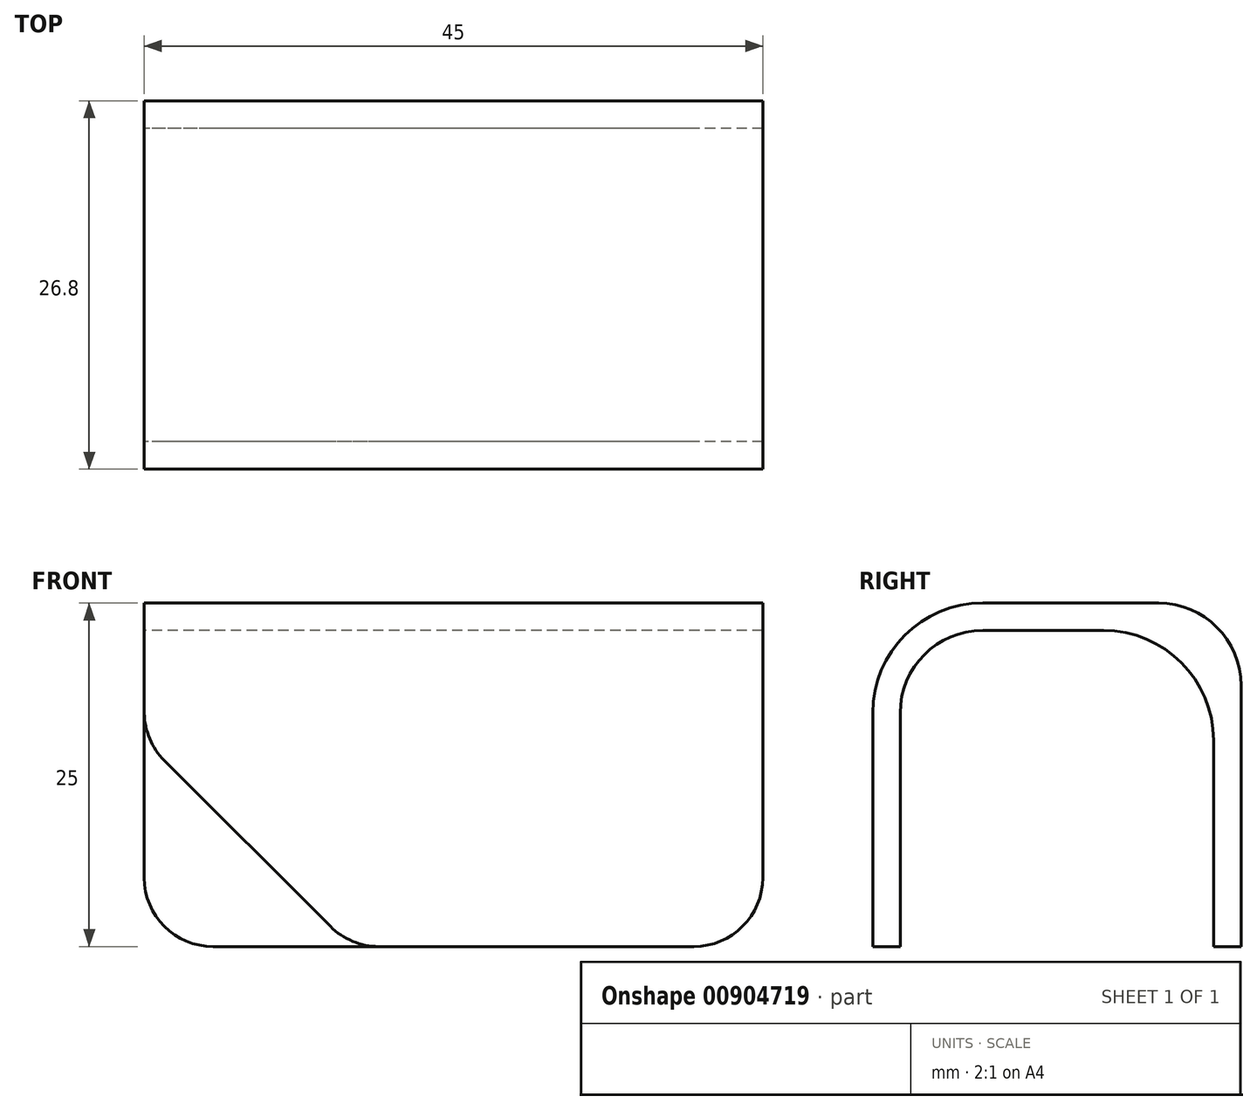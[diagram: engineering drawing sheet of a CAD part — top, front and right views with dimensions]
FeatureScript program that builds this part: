
annotation { "Feature Type Name" : "Feature", "Feature Type Description" : "" }
export const myFeature = defineFeature(function(context is Context, id is Id, definition is map)
    precondition{}
    {
        {
            var Q0;
            Q0=qCreatedBy(makeId("Right.planeOp"),FACE);
            var sketch = newSketch(context, id + "F0", { "sketchPlane" : qUnion([Q0])});
            skLineSegment(sketch, "E0.bottom", {"start": v(-13.4, 12.5) * mm, "end": v(13.4, 12.5) * mm});
            skLineSegment(sketch, "E0.top", {"start": v(-13.4, -12.5) * mm, "end": v(13.4, -12.5) * mm, "construction": true});
            skLineSegment(sketch, "E0.left", {"start": v(-13.4, 12.5) * mm, "end": v(-13.4, -12.5) * mm});
            skLineSegment(sketch, "E0.right", {"start": v(13.4, 12.5) * mm, "end": v(13.4, -12.5) * mm});
            skPoint(sketch, "E0.middle", {"position": v(0, 0) * mm});
            skLineSegment(sketch, "E1.0", {"start": v(11.4, 10.5) * mm, "end": v(11.4, -12.5) * mm});
            skLineSegment(sketch, "E1.1", {"start": v(-11.4, 10.5) * mm, "end": v(11.4, 10.5) * mm});
            skLineSegment(sketch, "E1.2", {"start": v(-11.4, 10.5) * mm, "end": v(-11.4, -12.5) * mm});
            skLineSegment(sketch, "E2", {"start": v(-11.4, -12.5) * mm, "end": v(-13.4, -12.5) * mm});
            skLineSegment(sketch, "E3", {"start": v(13.4, -12.5) * mm, "end": v(11.4, -12.5) * mm});
            skSolve(sketch);
        }
        {
            var Q0;
            Q0 = qSketchRegion(id + "F0", true);
            extrude(context, id + "F1", {"entities" : qUnion([Q0]), "depth" : 45 * mm, "offsetDistance" : 25 * mm});
        }
        {
            var Q0;
            Q0=makeQuery(id+"F1.opExtrude","SWEPT_EDGE",EDGE,{"disambiguationData":[OSD([sQuery(id+"F0.wireOp",EDGE,"E1.1"),sQuery(id+"F0.wireOp",EDGE,"E1.2")])]});
            fillet(context, id + "F2", {"entities" : qUnion([Q0]), "radius" : 6 * mm, "tangentPropagation" : true, "allowEdgeOverflow" : false});
        }
        {
            var Q0;
            Q0=makeQuery(id+"F1.opExtrude","SWEPT_EDGE",EDGE,{"disambiguationData":[OSD([sQuery(id+"F0.wireOp",EDGE,"E0.bottom"),sQuery(id+"F0.wireOp",EDGE,"E0.left")])]});
            fillet(context, id + "F3", {"entities" : qUnion([Q0]), "radius" : 8 * mm, "tangentPropagation" : true, "allowEdgeOverflow" : false});
        }
        {
            var Q0;
            Q0=makeQuery(id+"F1.opExtrude","CAP_EDGE",EDGE,{"disambiguationData":[OSD([sQuery(id+"F0.wireOp",EDGE,"E3")])],"isStart":true});
            var Q1;
            Q1=makeQuery(id+"F1.opExtrude","CAP_EDGE",EDGE,{"disambiguationData":[OSD([sQuery(id+"F0.wireOp",EDGE,"E3")])],"isStart":false});
            fillet(context, id + "F4", {"entities" : qUnion([Q0, Q1]), "radius" : 5 * mm, "tangentPropagation" : true, "allowEdgeOverflow" : false});
        }
        {
            var Q0;
            Q0=makeQuery(id+"F1.opExtrude","CAP_EDGE",EDGE,{"disambiguationData":[OSD([sQuery(id+"F0.wireOp",EDGE,"E2")])],"isStart":true});
            chamfer(context, id + "F5", {"entities" : qUnion([Q0]), "width" : 15 * mm, "tangentPropagation" : true});
        }
        {
            var Q0;
            {var subQ0=sQuery(id+"F0.wireOp",EDGE,"E2");Q0=makeQuery(id+"F5.opChamfer","BLEND_EDGE",EDGE,{"blendedFrom":[makeQuery(id+"F1.opExtrude","CAP_EDGE",EDGE,{"disambiguationData":[OSD([subQ0])],"isStart":true}),makeQuery(id+"F1.opExtrude","CAP_FACE",FACE,{"disambiguationData":[OSD([sQuery(id+"F0.wireOp",EDGE,"E0.bottom"),sQuery(id+"F0.wireOp",EDGE,"E0.left"),sQuery(id+"F0.wireOp",EDGE,"E0.right"),sQuery(id+"F0.wireOp",EDGE,"E1.0"),sQuery(id+"F0.wireOp",EDGE,"E1.1"),sQuery(id+"F0.wireOp",EDGE,"E1.2"),subQ0,sQuery(id+"F0.wireOp",EDGE,"E3")])],"isStart":true})],"blendedInto":[makeQuery(id+"F1.opExtrude","CAP_FACE",FACE,{"disambiguationData":[OSD([sQuery(id+"F0.wireOp",EDGE,"E0.bottom"),sQuery(id+"F0.wireOp",EDGE,"E0.left"),sQuery(id+"F0.wireOp",EDGE,"E0.right"),sQuery(id+"F0.wireOp",EDGE,"E1.0"),sQuery(id+"F0.wireOp",EDGE,"E1.1"),sQuery(id+"F0.wireOp",EDGE,"E1.2"),subQ0,sQuery(id+"F0.wireOp",EDGE,"E3")])],"isStart":true})]});}
            var Q1;
            {var subQ0=sQuery(id+"F0.wireOp",EDGE,"E2");Q1=makeQuery(id+"F5.opChamfer","BLEND_EDGE",EDGE,{"blendedFrom":[makeQuery(id+"F1.opExtrude","CAP_EDGE",EDGE,{"disambiguationData":[OSD([subQ0])],"isStart":true}),makeQuery(id+"F1.opExtrude","SWEPT_FACE",FACE,{"disambiguationData":[OSD([subQ0])]})],"blendedInto":[makeQuery(id+"F1.opExtrude","SWEPT_FACE",FACE,{"disambiguationData":[OSD([subQ0])]})]});}
            fillet(context, id + "F6", {"entities" : qUnion([Q0, Q1]), "radius" : 5 * mm, "tangentPropagation" : true, "allowEdgeOverflow" : false});
        }
        {
            var Q0;
            Q0=makeQuery(id+"F1.opExtrude","CAP_EDGE",EDGE,{"disambiguationData":[OSD([sQuery(id+"F0.wireOp",EDGE,"E2")])],"isStart":false});
            fillet(context, id + "F7", {"entities" : qUnion([Q0]), "radius" : 5 * mm, "tangentPropagation" : true, "allowEdgeOverflow" : false});
        }
        {
            var Q0;
            Q0=makeQuery(id+"F1.opExtrude","SWEPT_EDGE",EDGE,{"disambiguationData":[OSD([sQuery(id+"F0.wireOp",EDGE,"E1.0"),sQuery(id+"F0.wireOp",EDGE,"E1.1")])]});
            fillet(context, id + "F8", {"entities" : qUnion([Q0]), "radius" : 8 * mm, "tangentPropagation" : true, "allowEdgeOverflow" : false});
        }
        {
            var Q0;
            Q0=makeQuery(id+"F1.opExtrude","SWEPT_EDGE",EDGE,{"disambiguationData":[OSD([sQuery(id+"F0.wireOp",EDGE,"E0.bottom"),sQuery(id+"F0.wireOp",EDGE,"E0.right")])]});
            fillet(context, id + "F9", {"entities" : qUnion([Q0]), "radius" : 6 * mm, "tangentPropagation" : true, "allowEdgeOverflow" : false});
        }
    });
